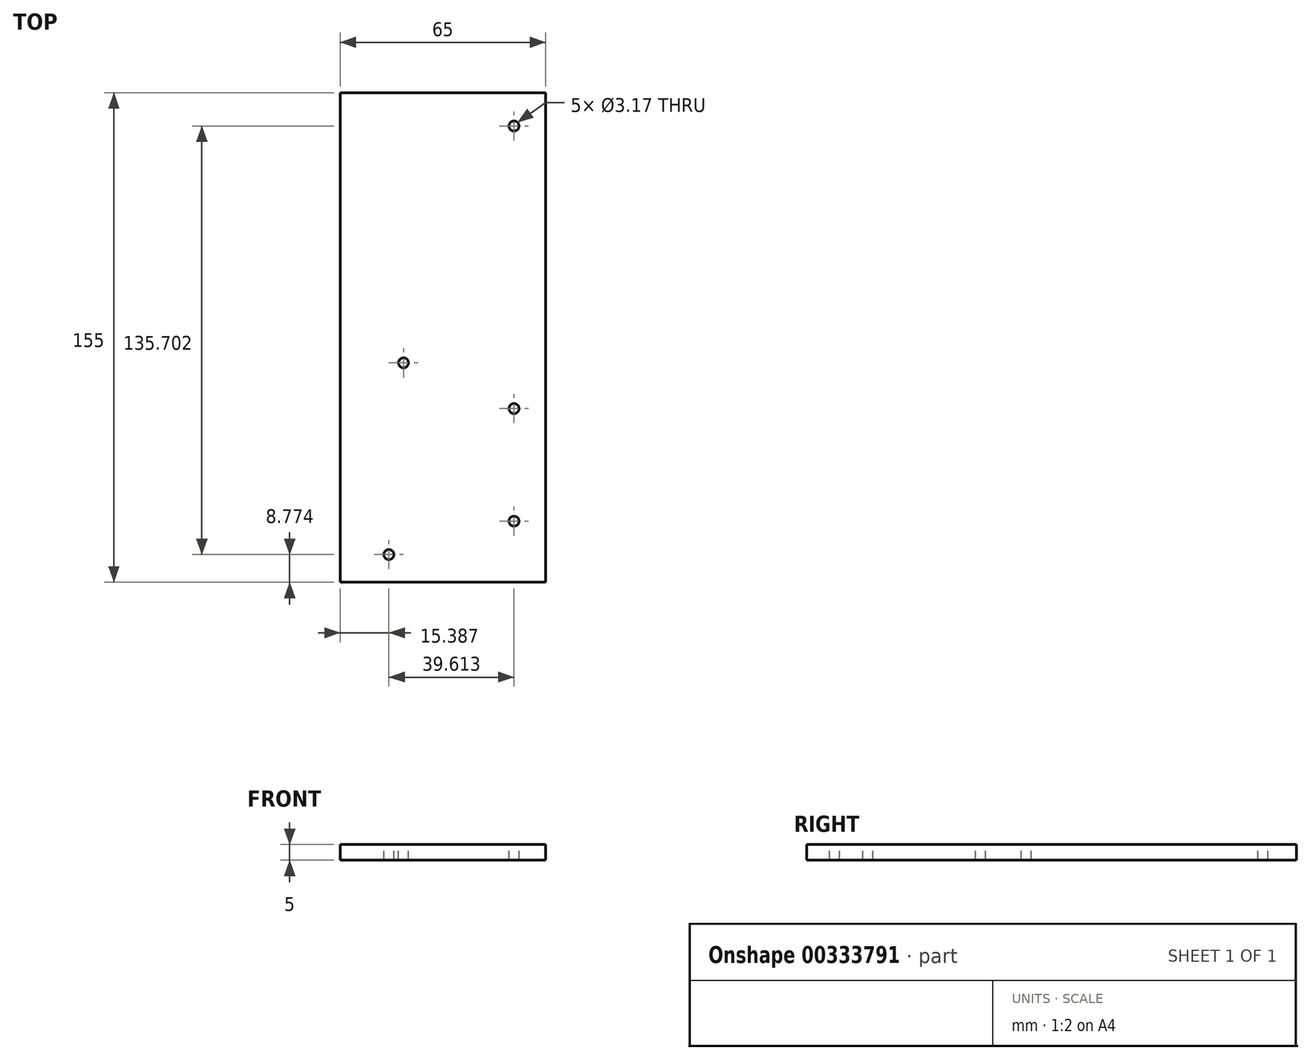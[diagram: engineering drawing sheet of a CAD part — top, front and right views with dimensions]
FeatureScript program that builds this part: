
annotation { "Feature Type Name" : "Feature", "Feature Type Description" : "" }
export const myFeature = defineFeature(function(context is Context, id is Id, definition is map)
    precondition{}
    {
        {
            var Q0;
            Q0=qCreatedBy(makeId("Top.planeOp"),FACE);
            var sketch = newSketch(context, id + "F0", { "sketchPlane" : qUnion([Q0])});
            skLineSegment(sketch, "E0.bottom", {"start": v(100, 100) * mm, "end": v(-100, 100) * mm});
            skLineSegment(sketch, "E0.top", {"start": v(100, -100) * mm, "end": v(-100, -100) * mm});
            skLineSegment(sketch, "E0.left", {"start": v(100, 100) * mm, "end": v(100, -100) * mm});
            skLineSegment(sketch, "E0.right", {"start": v(-100, 100) * mm, "end": v(-100, -100) * mm});
            skPoint(sketch, "E0.middle", {"position": v(0, 0) * mm});
            skSolve(sketch);
        }
        {
            var Q0;
            Q0=qSketchRegion(id+"F0",true);
            extrude(context, id + "F1", {"entities" : qUnion([Q0]), "depth" : 5 * mm});
        }
        {
            var Q0;
            Q0=makeQuery(id+"F1.opExtrude","CAP_FACE",FACE,{"disambiguationData":[OSD([sQuery(id+"F0.wireOp",EDGE,"E0.bottom"),sQuery(id+"F0.wireOp",EDGE,"E0.top"),sQuery(id+"F0.wireOp",EDGE,"E0.left"),sQuery(id+"F0.wireOp",EDGE,"E0.right")])],"isStart":false});
            var sketch = newSketch(context, id + "F2", { "sketchPlane" : qUnion([Q0])});
            skCircle(sketch, "E1", {"center": v(0, 0) * mm, "radius": 1.59 * mm});
            skCircle(sketch, "E2", {"center": v(0, -35.65) * mm, "radius": 1.59 * mm});
            skCircle(sketch, "E3", {"center": v(-39.61, -46.23) * mm, "radius": 1.59 * mm});
            skCircle(sketch, "E4", {"center": v(-35, 14.48) * mm, "radius": 1.59 * mm});
            skCircle(sketch, "E5", {"center": v(0, 89.48) * mm, "radius": 1.59 * mm});
            skSolve(sketch);
        }
        {
            var Q0;
            Q0=qSketchRegion(id+"F2",true);
            extrude(context, id + "F3", {"entities" : qUnion([Q0]), "operationType" : NewBodyOperationType.REMOVE, "endBound" : BoundingType.THROUGH_ALL, "oppositeDirection" : true, "depth" : 25 * mm});
        }
        {
            var Q0;
            Q0=makeQuery(id+"F1.opExtrude","CAP_FACE",FACE,{"disambiguationData":[OSD([sQuery(id+"F0.wireOp",EDGE,"E0.bottom"),sQuery(id+"F0.wireOp",EDGE,"E0.top"),sQuery(id+"F0.wireOp",EDGE,"E0.left"),sQuery(id+"F0.wireOp",EDGE,"E0.right")])],"isStart":false});
            var sketch = newSketch(context, id + "F4", { "sketchPlane" : qUnion([Q0])});
            skLineSegment(sketch, "E6.bottom", {"start": v(-55, 100) * mm, "end": v(10, 100) * mm});
            skLineSegment(sketch, "E6.top", {"start": v(-55, -55) * mm, "end": v(10, -55) * mm});
            skLineSegment(sketch, "E6.left", {"start": v(-55, 100) * mm, "end": v(-55, -55) * mm});
            skLineSegment(sketch, "E6.right", {"start": v(10, 100) * mm, "end": v(10, -55) * mm});
            skLineSegment(sketch, "E7.bottom", {"start": v(-100, 100) * mm, "end": v(100, 100) * mm});
            skLineSegment(sketch, "E7.top", {"start": v(-100, -100) * mm, "end": v(100, -100) * mm});
            skLineSegment(sketch, "E7.left", {"start": v(-100, 100) * mm, "end": v(-100, -100) * mm});
            skLineSegment(sketch, "E7.right", {"start": v(100, 100) * mm, "end": v(100, -100) * mm});
            skSolve(sketch);
        }
        {
            var Q0;
            Q0=makeQuery(id+"F4.imprint","IMPRINT",FACE,{"disambiguationData":[TD([[makeQuery(id+"F4.imprint","IMPRINT",EDGE,{"derivedFrom":sQuery(id+"F4.wireOp",EDGE,"E6.top")}),-1.0]])]});
            var Q1;
            Q1=makeQuery(id+"F4.imprint","IMPRINT",FACE,{"disambiguationData":[TD([[makeQuery(id+"F4.imprint","IMPRINT",EDGE,{"derivedFrom":makeQuery(id+"F3.boolean.opBoolean","COPY",EDGE,{"derivedFrom":makeQuery(id+"F3.opExtrude","CAP_EDGE",EDGE,{"disambiguationData":[OSD([sQuery(id+"F2.wireOp",EDGE,"E1")])],"isStart":true})})}),1.0]])]});
            var Q2;
            Q2=makeQuery(id+"F4.imprint","IMPRINT",FACE,{"disambiguationData":[TD([[makeQuery(id+"F4.imprint","IMPRINT",EDGE,{"derivedFrom":makeQuery(id+"F3.boolean.opBoolean","COPY",EDGE,{"derivedFrom":makeQuery(id+"F3.opExtrude","CAP_EDGE",EDGE,{"disambiguationData":[OSD([sQuery(id+"F2.wireOp",EDGE,"E2")])],"isStart":true})})}),1.0]])]});
            var Q3;
            Q3=makeQuery(id+"F4.imprint","IMPRINT",FACE,{"disambiguationData":[TD([[makeQuery(id+"F4.imprint","IMPRINT",EDGE,{"derivedFrom":makeQuery(id+"F3.boolean.opBoolean","COPY",EDGE,{"derivedFrom":makeQuery(id+"F3.opExtrude","CAP_EDGE",EDGE,{"disambiguationData":[OSD([sQuery(id+"F2.wireOp",EDGE,"E3")])],"isStart":true})})}),1.0]])]});
            var Q4;
            Q4=makeQuery(id+"F4.imprint","IMPRINT",FACE,{"disambiguationData":[TD([[makeQuery(id+"F4.imprint","IMPRINT",EDGE,{"derivedFrom":makeQuery(id+"F3.boolean.opBoolean","COPY",EDGE,{"derivedFrom":makeQuery(id+"F3.opExtrude","CAP_EDGE",EDGE,{"disambiguationData":[OSD([sQuery(id+"F2.wireOp",EDGE,"E4")])],"isStart":true})})}),1.0]])]});
            var Q5;
            Q5=makeQuery(id+"F4.imprint","IMPRINT",FACE,{"disambiguationData":[TD([[makeQuery(id+"F4.imprint","IMPRINT",EDGE,{"derivedFrom":makeQuery(id+"F3.boolean.opBoolean","COPY",EDGE,{"derivedFrom":makeQuery(id+"F3.opExtrude","CAP_EDGE",EDGE,{"disambiguationData":[OSD([sQuery(id+"F2.wireOp",EDGE,"E5")])],"isStart":true})})}),1.0]])]});
            extrude(context, id + "F5", {"entities" : qUnion([Q0, Q1, Q2, Q3, Q4, Q5]), "operationType" : NewBodyOperationType.REMOVE, "oppositeDirection" : true, "depth" : 25 * mm});
        }
    });
